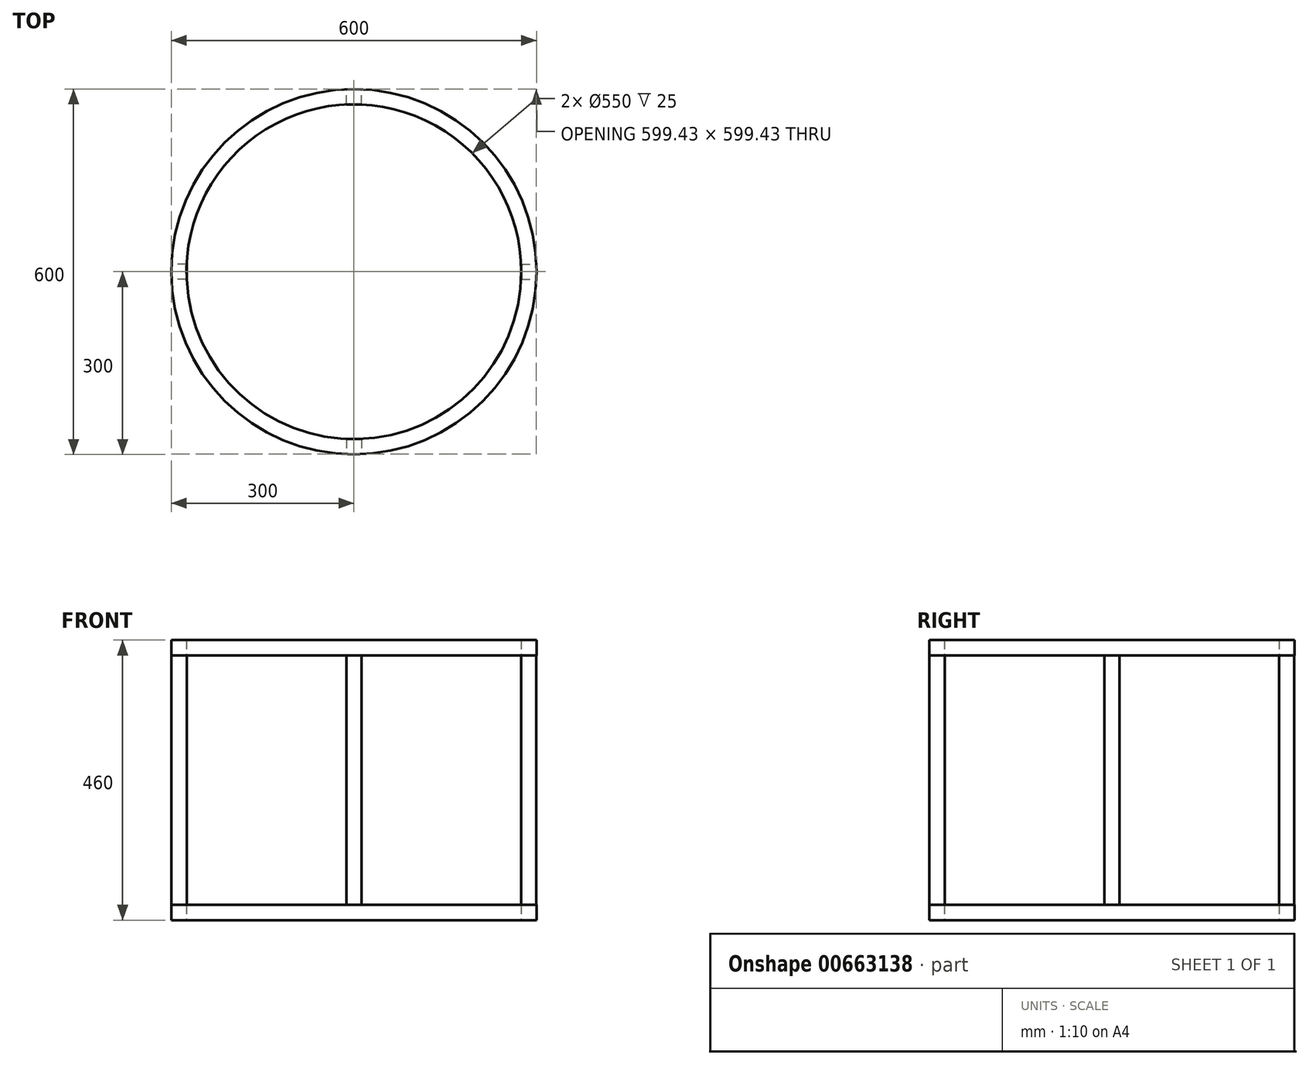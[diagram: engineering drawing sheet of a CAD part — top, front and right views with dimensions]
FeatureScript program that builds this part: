
annotation { "Feature Type Name" : "Feature", "Feature Type Description" : "" }
export const myFeature = defineFeature(function(context is Context, id is Id, definition is map)
    precondition{}
    {
        {
            var Q0;
            Q0=qCreatedBy(makeId("Top.planeOp"),FACE);
            var sketch = newSketch(context, id + "F0", { "sketchPlane" : qUnion([Q0])});
            skCircle(sketch, "E0", {"center": v(0, 0) * mm, "radius": 300 * mm});
            skSolve(sketch);
        }
        {
            var Q0;
            Q0=makeQuery(id+"F0.imprint","IMPRINT",FACE,{"disambiguationData":[TD([[makeQuery(id+"F0.imprint","IMPRINT",EDGE,{"derivedFrom":sQuery(id+"F0.wireOp",EDGE,"E0")}),1.0]])]});
            var sketch = newSketch(context, id + "F1", { "sketchPlane" : qUnion([Q0])});
            skCircle(sketch, "E1", {"center": v(0, 0) * mm, "radius": 275 * mm});
            skSolve(sketch);
        }
        {
            var Q0;
            Q0=makeQuery(id+"F1.imprint","IMPRINT",FACE,{"disambiguationData":[TD([[makeQuery(id+"F1.imprint","IMPRINT",EDGE,{"derivedFrom":sQuery(id+"F1.wireOp",EDGE,"E1")}),-1.0]])]});
            extrude(context, id + "F2", {"entities" : qUnion([Q0]), "depth" : 25 * mm, "offsetDistance" : 25 * mm});
        }
        {
            var Q0;
            Q0=makeQuery(id+"F2.opExtrude","CAP_FACE",FACE,{"disambiguationData":[OSD([sQuery(id+"F0.wireOp",EDGE,"E0"),sQuery(id+"F1.wireOp",EDGE,"E1")])],"isStart":false});
            var sketch = newSketch(context, id + "F3", { "sketchPlane" : qUnion([Q0])});
            skLineSegment(sketch, "E2.bottom", {"start": v(12.5, 274.72) * mm, "end": v(-12.5, 274.72) * mm});
            skLineSegment(sketch, "E2.top", {"start": v(12.5, 299.72) * mm, "end": v(-12.5, 299.72) * mm});
            skLineSegment(sketch, "E2.left", {"start": v(12.5, 274.72) * mm, "end": v(12.5, 299.72) * mm});
            skLineSegment(sketch, "E2.right", {"start": v(-12.5, 274.72) * mm, "end": v(-12.5, 299.72) * mm});
            skPoint(sketch, "E2.middle", {"position": v(0, 287.22) * mm});
            skLineSegment(sketch, "E3.1.0", {"start": v(-299.72, 12.5) * mm, "end": v(-299.72, -12.5) * mm});
            skLineSegment(sketch, "E3.1.1", {"start": v(-274.72, -12.5) * mm, "end": v(-299.72, -12.5) * mm});
            skLineSegment(sketch, "E3.1.2", {"start": v(-274.72, 12.5) * mm, "end": v(-299.72, 12.5) * mm});
            skLineSegment(sketch, "E3.1.3", {"start": v(-274.72, 12.5) * mm, "end": v(-274.72, -12.5) * mm});
            skPoint(sketch, "E3.1.4", {"position": v(-287.22, 0) * mm});
            skLineSegment(sketch, "E3.2.0", {"start": v(-12.5, -299.72) * mm, "end": v(12.5, -299.72) * mm});
            skLineSegment(sketch, "E3.2.1", {"start": v(12.5, -274.72) * mm, "end": v(12.5, -299.72) * mm});
            skLineSegment(sketch, "E3.2.2", {"start": v(-12.5, -274.72) * mm, "end": v(-12.5, -299.72) * mm});
            skLineSegment(sketch, "E3.2.3", {"start": v(-12.5, -274.72) * mm, "end": v(12.5, -274.72) * mm});
            skPoint(sketch, "E3.2.4", {"position": v(0, -287.22) * mm});
            skLineSegment(sketch, "E3.3.0", {"start": v(299.72, -12.5) * mm, "end": v(299.72, 12.5) * mm});
            skLineSegment(sketch, "E3.3.1", {"start": v(274.72, 12.5) * mm, "end": v(299.72, 12.5) * mm});
            skLineSegment(sketch, "E3.3.2", {"start": v(274.72, -12.5) * mm, "end": v(299.72, -12.5) * mm});
            skLineSegment(sketch, "E3.3.3", {"start": v(274.72, -12.5) * mm, "end": v(274.72, 12.5) * mm});
            skPoint(sketch, "E3.3.4", {"position": v(287.22, 0) * mm});
            skPoint(sketch, "E3.center", {"position": v(0, 0) * mm});
            skSolve(sketch);
        }
        {
            var Q0;
            Q0 = qSketchRegion(id + "F3", true);
            extrude(context, id + "F4", {"entities" : qUnion([Q0]), "operationType" : NewBodyOperationType.ADD, "depth" : 410 * mm, "offsetDistance" : 25 * mm});
        }
        {
            var Q0;
            Q0=qCreatedBy(makeId("Top.planeOp"),FACE);
            cPlane(context, id + "F5", {"entities" : qUnion([Q0]), "cplaneType" : CPlaneType.OFFSET, "offset" : 435 * mm, "width" : 150 * mm, "height" : 150 * mm});
        }
        {
            var Q0;
            Q0=qCreatedBy(id+"F5.planeOp",FACE);
            var sketch = newSketch(context, id + "F6", { "sketchPlane" : qUnion([Q0])});
            skCircle(sketch, "E4", {"center": v(0, 0) * mm, "radius": 300 * mm});
            skCircle(sketch, "E5", {"center": v(0, 0) * mm, "radius": 275 * mm});
            skSolve(sketch);
        }
        {
            var Q0;
            Q0=makeQuery(id+"F6.imprint","IMPRINT",FACE,{"disambiguationData":[TD([[makeQuery(id+"F6.imprint","IMPRINT",EDGE,{"derivedFrom":sQuery(id+"F6.wireOp",EDGE,"E4")}),1.0]])]});
            extrude(context, id + "F7", {"entities" : qUnion([Q0]), "operationType" : NewBodyOperationType.ADD, "depth" : 25 * mm, "offsetDistance" : 25 * mm});
        }
    });
